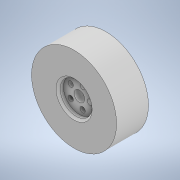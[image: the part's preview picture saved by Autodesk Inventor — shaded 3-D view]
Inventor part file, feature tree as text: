
AUTODESK INVENTOR PART (.ipt)
format: ipt  version: 2021 (Build 250183000, 183)  size: 143,360 bytes
history: native  units: mm
features: sketch x6, extrude x5, chamfer x1
ambient origin geometry x8: Origin, YZ Plane, XZ Plane, XY Plane, X Axis, Y Axis, Z Axis, Center Point
bodies: Body1 (feature_tree)
feature tree (12):
  sketch  "Sketch28"  dims[d84=80.0mm d85=30.0mm d86=0.0mm]
  extrude  "Extrusion25"  Depth=30.0mm TaperAngle=0.0deg
  extrude  "Extrusion26"  Depth=5.0mm TaperAngle=0.0deg
  extrude  "Extrusion27"  Depth=5.0mm TaperAngle=0.0deg
  extrude  "Extrusion28"  Depth=20.0mm TaperAngle=0.0deg
  extrude  "Extrusion29"  Depth=20.0mm TaperAngle=360.0deg
  chamfer  "Chamfer1"  Distance=20.0mm
  sketch  "Sketch29"  dims[d87=30.0mm d88=5.0mm d89=0.0mm]
  sketch  "Sketch30"  dims[d90=30.0mm d91=5.0mm d92=0.0mm]
  sketch  "Sketch31"  dims[d93=10.0mm d94=20.0mm d95=0.0mm]
  sketch  "Sketch32"  dims[d96=5.0mm d97=50.0mm d99=360.0deg d101=20.0mm d102=0.0mm]
  sketch  "Sketch33"  dims[d103=2.0mm d104=2.0mm d105=45.0deg d41=0.5mm d42=0.872665mm d43=0.5mm d44=0.872665mm d74=0.5mm d75=0.872665mm d76=0.5mm d77=0.872665mm]
